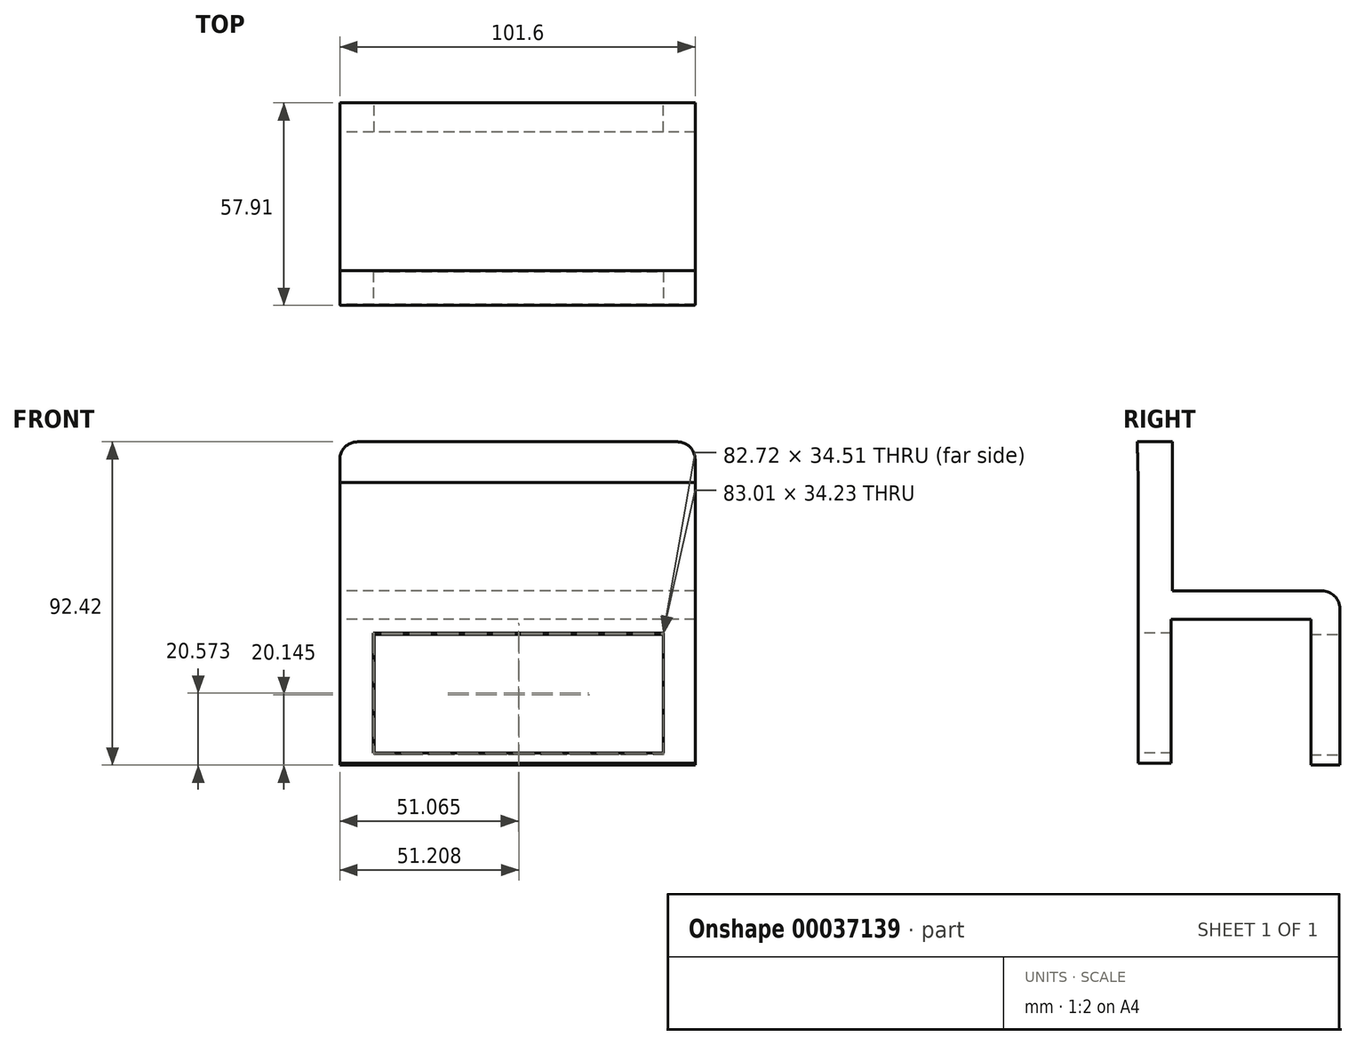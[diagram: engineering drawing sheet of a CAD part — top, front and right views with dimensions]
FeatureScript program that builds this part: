
annotation { "Feature Type Name" : "Feature", "Feature Type Description" : "" }
export const myFeature = defineFeature(function(context is Context, id is Id, definition is map)
    precondition{}
    {
        {
            var Q0;
            Q0=qCreatedBy(makeId("Right.planeOp"),FACE);
            var sketch = newSketch(context, id + "F0", { "sketchPlane" : qUnion([Q0])});
            skLineSegment(sketch, "E0", {"start": v(-64.07, 30.92) * mm, "end": v(-64.07, -49.23) * mm});
            skLineSegment(sketch, "E1", {"start": v(-64.07, -49.23) * mm, "end": v(-54.66, -49.23) * mm});
            skLineSegment(sketch, "E2", {"start": v(-54.66, -49.23) * mm, "end": v(-54.66, -8.16) * mm});
            skLineSegment(sketch, "E3", {"start": v(-54.66, -8.16) * mm, "end": v(-14.72, -8.16) * mm});
            skLineSegment(sketch, "E4", {"start": v(-14.72, -8.16) * mm, "end": v(-14.72, -49.8) * mm});
            skLineSegment(sketch, "E5", {"start": v(-14.72, -49.8) * mm, "end": v(-6.45, -49.8) * mm});
            skLineSegment(sketch, "E6", {"start": v(-6.45, -49.8) * mm, "end": v(-6.45, -7.59) * mm});
            skLineSegment(sketch, "E7", {"start": v(-6.45, -7.59) * mm, "end": v(-6.45, 0) * mm});
            skLineSegment(sketch, "E8", {"start": v(-6.45, 0) * mm, "end": v(-54.37, 0) * mm});
            skLineSegment(sketch, "E9", {"start": v(-54.37, 0) * mm, "end": v(-54.37, 42.61) * mm});
            skLineSegment(sketch, "E10", {"start": v(-54.37, 42.61) * mm, "end": v(-64.36, 42.61) * mm});
            skLineSegment(sketch, "E11", {"start": v(-64.36, 42.61) * mm, "end": v(-64.07, 30.92) * mm});
            skSolve(sketch);
        }
        {
            var Q0;
            Q0=makeQuery(id+"F0.imprint","IMPRINT",FACE,{"disambiguationData":[TD([[makeQuery(id+"F0.imprint","IMPRINT",EDGE,{"derivedFrom":sQuery(id+"F0.wireOp",EDGE,"E0")}),1.0]])]});
            extrude(context, id + "F1", {"entities" : qUnion([Q0]), "depth" : 101.6 * mm});
        }
        {
            var Q0;
            Q0=makeQuery(id+"F1.opExtrude","CAP_EDGE",EDGE,{"disambiguationData":[OSD([sQuery(id+"F0.wireOp",EDGE,"E10")])],"isStart":false});
            var Q1;
            Q1=makeQuery(id+"F1.opExtrude","CAP_EDGE",EDGE,{"disambiguationData":[OSD([sQuery(id+"F0.wireOp",EDGE,"E10")])],"isStart":true});
            var Q2;
            Q2=makeQuery(id+"F1.opExtrude","SWEPT_EDGE",EDGE,{"disambiguationData":[OSD([sQuery(id+"F0.wireOp",EDGE,"E7"),sQuery(id+"F0.wireOp",EDGE,"E8")])]});
            fillet(context, id + "F2", {"entities" : qUnion([Q0, Q1, Q2]), "radius" : 5.08 * mm, "tangentPropagation" : true, "allowEdgeOverflow" : false});
        }
        {
            var Q0;
            Q0=makeQuery(id+"F1.opExtrude","SWEPT_FACE",FACE,{"disambiguationData":[OSD([sQuery(id+"F0.wireOp",EDGE,"E6"),sQuery(id+"F0.wireOp",EDGE,"E7")])]});
            var sketch = newSketch(context, id + "F3", { "sketchPlane" : qUnion([Q0])});
            skLineSegment(sketch, "E12.bottom", {"start": v(-92.57, -12.4) * mm, "end": v(-9.85, -12.4) * mm});
            skLineSegment(sketch, "E12.top", {"start": v(-92.57, -46.92) * mm, "end": v(-9.85, -46.92) * mm});
            skLineSegment(sketch, "E12.left", {"start": v(-92.57, -12.4) * mm, "end": v(-92.57, -46.92) * mm});
            skLineSegment(sketch, "E12.right", {"start": v(-9.85, -12.4) * mm, "end": v(-9.85, -46.92) * mm});
            skSolve(sketch);
        }
        {
            var Q0;
            Q0=makeQuery(id+"F1.opExtrude","SWEPT_FACE",FACE,{"disambiguationData":[OSD([sQuery(id+"F0.wireOp",EDGE,"E0")])]});
            var sketch = newSketch(context, id + "F4", { "sketchPlane" : qUnion([Q0])});
            skLineSegment(sketch, "E13.bottom", {"start": v(9.56, -12.12) * mm, "end": v(92.57, -12.12) * mm});
            skLineSegment(sketch, "E13.top", {"start": v(9.56, -46.35) * mm, "end": v(92.57, -46.35) * mm});
            skLineSegment(sketch, "E13.left", {"start": v(9.56, -12.12) * mm, "end": v(9.56, -46.35) * mm});
            skLineSegment(sketch, "E13.right", {"start": v(92.57, -12.12) * mm, "end": v(92.57, -46.35) * mm});
            skSolve(sketch);
        }
        {
            var Q0;
            Q0 = qSketchRegion(id + "F4", true);
            extrude(context, id + "F5", {"entities" : qUnion([Q0]), "operationType" : NewBodyOperationType.REMOVE, "oppositeDirection" : true, "depth" : 25.4 * mm});
        }
        {
            var Q0;
            Q0=makeQuery(id+"F3.imprint","IMPRINT",FACE,{"disambiguationData":[TD([[makeQuery(id+"F3.imprint","IMPRINT",EDGE,{"derivedFrom":sQuery(id+"F3.wireOp",EDGE,"E12.bottom")}),-1.0]])]});
            extrude(context, id + "F6", {"entities" : qUnion([Q0]), "operationType" : NewBodyOperationType.REMOVE, "oppositeDirection" : true, "depth" : 25.4 * mm});
        }
    });
